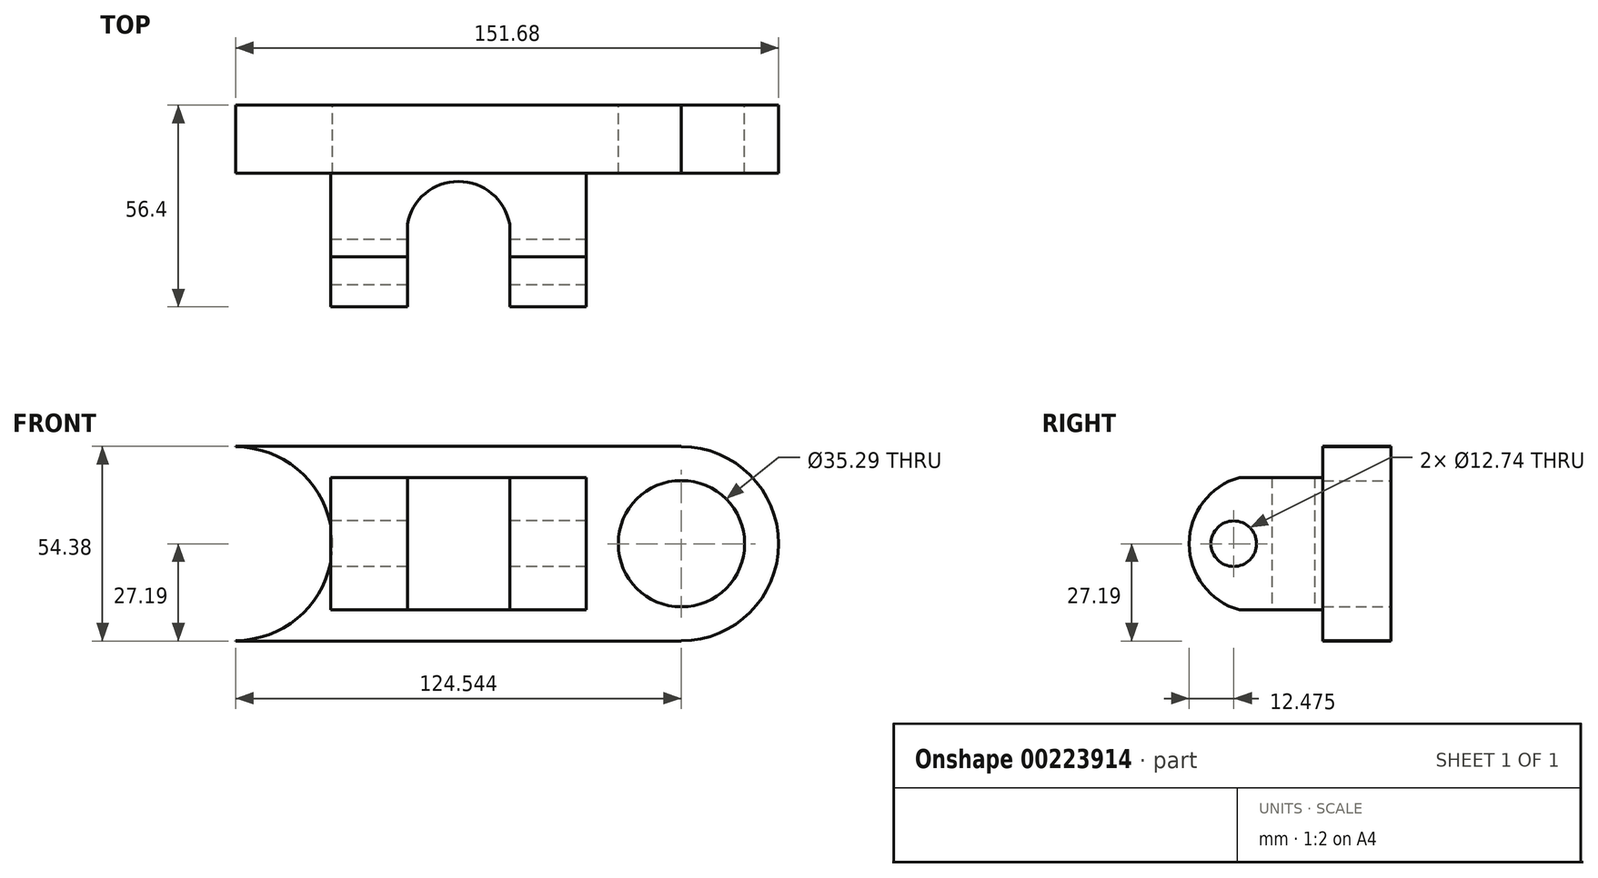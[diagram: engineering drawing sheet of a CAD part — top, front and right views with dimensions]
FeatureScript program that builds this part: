
annotation { "Feature Type Name" : "Feature", "Feature Type Description" : "" }
export const myFeature = defineFeature(function(context is Context, id is Id, definition is map)
    precondition{}
    {
        {
            var Q0;
            Q0=qCreatedBy(makeId("Front.planeOp"),FACE);
            var sketch = newSketch(context, id + "F0", { "sketchPlane" : qUnion([Q0])});
            skLineSegment(sketch, "E0.bottom", {"start": v(-62.27, 27.2) * mm, "end": v(62.27, 27.2) * mm});
            skLineSegment(sketch, "E0.top", {"start": v(-62.27, -27.2) * mm, "end": v(62.27, -27.2) * mm});
            skLineSegment(sketch, "E0.left", {"start": v(-62.27, 27.2) * mm, "end": v(-62.27, -27.2) * mm});
            skLineSegment(sketch, "E0.right", {"start": v(62.27, 27.2) * mm, "end": v(62.27, -27.2) * mm});
            skPoint(sketch, "E0.middle", {"position": v(0, 0) * mm});
            skCircle(sketch, "E1", {"center": v(-62.27, 0) * mm, "radius": 27.08 * mm});
            skCircle(sketch, "E2", {"center": v(62.27, 0) * mm, "radius": 27.13 * mm});
            skCircle(sketch, "E3", {"center": v(-62.27, 0) * mm, "radius": 16.55 * mm});
            skCircle(sketch, "E4", {"center": v(62.27, 0) * mm, "radius": 17.64 * mm});
            skPoint(sketch, "E5.bottom.end.orphan", {"position": v(-23.15, 9.85) * mm});
            skPoint(sketch, "E5.top.end.orphan", {"position": v(-23.15, -9.85) * mm});
            skPoint(sketch, "E5.left.end.orphan", {"position": v(23.15, -9.85) * mm});
            skPoint(sketch, "E5.left.start.orphan", {"position": v(23.15, 9.85) * mm});
            skPoint(sketch, "E6.top.start.orphan", {"position": v(27.33, -15.1) * mm});
            skPoint(sketch, "E6.bottom.start.orphan", {"position": v(27.33, 15.1) * mm});
            skPoint(sketch, "E6.right.end.orphan", {"position": v(-27.33, -15.1) * mm});
            skPoint(sketch, "E6.right.start.orphan", {"position": v(-27.33, 15.1) * mm});
            skSolve(sketch);
        }
        {
            var Q0;
            {var subQ5=sQuery(id+"F0.wireOp",EDGE,"E0.bottom");Q0=makeQuery(id+"F0.imprint","IMPRINT",FACE,{"disambiguationData":[TD([[makeQuery(id+"F0.imprint","IMPRINT",EDGE,{"derivedFrom":subQ5}),-1.0]])]});}
            var Q1;
            {var subQ0=sQuery(id+"F0.wireOp",EDGE,"E1");var subQ1=sQuery(id+"F0.wireOp",EDGE,"E0.left");var subQ2=makeQuery(id+"F0.imprint","INTERSECT",VERTEX,{"disambiguationData":[OD(0.0)],"derivedFrom":[subQ1,subQ0]});Q1=makeQuery(id+"F0.imprint","IMPRINT",FACE,{"disambiguationData":[TD([[makeQuery(id+"F0.imprint","IMPRINT",EDGE,{"disambiguationData":[TD([[subQ2,-1.0]])],"derivedFrom":subQ1}),1.0]])]});}
            var Q2;
            {var subQ0=sQuery(id+"F0.wireOp",EDGE,"E1");var subQ1=sQuery(id+"F0.wireOp",EDGE,"E0.left");var subQ2=makeQuery(id+"F0.imprint","INTERSECT",VERTEX,{"disambiguationData":[OD(0.0)],"derivedFrom":[subQ1,subQ0]});Q2=makeQuery(id+"F0.imprint","IMPRINT",FACE,{"disambiguationData":[TD([[makeQuery(id+"F0.imprint","IMPRINT",EDGE,{"disambiguationData":[TD([[subQ2,-1.0]])],"derivedFrom":subQ1}),-1.0]])]});}
            var Q3;
            {var subQ0=sQuery(id+"F0.wireOp",EDGE,"E2");var subQ1=sQuery(id+"F0.wireOp",EDGE,"E0.right");var subQ2=makeQuery(id+"F0.imprint","INTERSECT",VERTEX,{"disambiguationData":[OD(0.0)],"derivedFrom":[subQ1,subQ0]});Q3=makeQuery(id+"F0.imprint","IMPRINT",FACE,{"disambiguationData":[TD([[makeQuery(id+"F0.imprint","IMPRINT",EDGE,{"disambiguationData":[TD([[subQ2,-1.0]])],"derivedFrom":subQ1}),-1.0]])]});}
            var Q4;
            {var subQ0=sQuery(id+"F0.wireOp",EDGE,"E2");var subQ1=sQuery(id+"F0.wireOp",EDGE,"E0.right");var subQ2=makeQuery(id+"F0.imprint","INTERSECT",VERTEX,{"disambiguationData":[OD(0.0)],"derivedFrom":[subQ1,subQ0]});Q4=makeQuery(id+"F0.imprint","IMPRINT",FACE,{"disambiguationData":[TD([[makeQuery(id+"F0.imprint","IMPRINT",EDGE,{"disambiguationData":[TD([[subQ2,-1.0]])],"derivedFrom":subQ1}),1.0]])]});}
            extrude(context, id + "F1", {"entities" : qUnion([Q0, Q1, Q2, Q3, Q4]), "depth" : 19.05 * mm});
        }
        {
            var Q0;
            Q0=makeQuery(id+"F1.opExtrude","CAP_FACE",FACE,{"disambiguationData":[OSD([sQuery(id+"F0.wireOp",EDGE,"E0.bottom"),sQuery(id+"F0.wireOp",EDGE,"E0.top"),sQuery(id+"F0.wireOp",EDGE,"E0.left"),sQuery(id+"F0.wireOp",EDGE,"E0.right"),sQuery(id+"F0.wireOp",EDGE,"E1"),sQuery(id+"F0.wireOp",EDGE,"E2"),sQuery(id+"F0.wireOp",EDGE,"E3"),sQuery(id+"F0.wireOp",EDGE,"E4")])],"isStart":false});
            var sketch = newSketch(context, id + "F2", { "sketchPlane" : qUnion([Q0])});
            skLineSegment(sketch, "E7.bottom", {"start": v(-35.7, 18.52) * mm, "end": v(35.7, 18.52) * mm});
            skLineSegment(sketch, "E7.top", {"start": v(-35.7, -18.52) * mm, "end": v(35.7, -18.52) * mm});
            skLineSegment(sketch, "E7.left", {"start": v(-35.7, 18.52) * mm, "end": v(-35.7, -18.52) * mm});
            skLineSegment(sketch, "E7.right", {"start": v(35.7, 18.52) * mm, "end": v(35.7, -18.52) * mm});
            skPoint(sketch, "E7.middle", {"position": v(0, 0) * mm});
            skSolve(sketch);
        }
        {
            var Q0;
            Q0 = qSketchRegion(id + "F2", true);
            extrude(context, id + "F3", {"entities" : qUnion([Q0]), "operationType" : NewBodyOperationType.ADD, "depth" : 38.1 * mm});
        }
        {
            var Q0;
            Q0=makeQuery(id+"F3.opExtrude","SWEPT_FACE",FACE,{"disambiguationData":[OSD([sQuery(id+"F2.wireOp",EDGE,"E7.right")])]});
            var sketch = newSketch(context, id + "F4", { "sketchPlane" : qUnion([Q0])});
            skArc(sketch, "E8", {"start": v(-42.34, 18.52) * mm, "mid": v(-56.4, 0) * mm, "end": v(-42.34, -18.52) * mm});
            skSolve(sketch);
        }
        {
            var Q0;
            {var subQ0=sQuery(id+"F4.wireOp",EDGE,"E8");Q0=makeQuery(id+"F4.imprint","IMPRINT",FACE,{"disambiguationData":[TD([[makeQuery(id+"F4.imprint","IMPRINT",EDGE,{"derivedFrom":subQ0}),-1.0]])]});}
            extrude(context, id + "F5", {"entities" : qUnion([Q0]), "operationType" : NewBodyOperationType.REMOVE, "endBound" : BoundingType.THROUGH_ALL, "oppositeDirection" : true, "depth" : 25.4 * mm});
        }
        {
            var Q0;
            Q0=makeQuery(id+"F3.opExtrude","SWEPT_FACE",FACE,{"disambiguationData":[OSD([sQuery(id+"F2.wireOp",EDGE,"E7.top")])]});
            var sketch = newSketch(context, id + "F6", { "sketchPlane" : qUnion([Q0])});
            skLineSegment(sketch, "E9.bottom", {"start": v(-14.3, 60.64) * mm, "end": v(14.3, 60.64) * mm});
            skLineSegment(sketch, "E9.top", {"start": v(-14.3, 33.27) * mm, "end": v(14.3, 33.27) * mm});
            skLineSegment(sketch, "E9.left", {"start": v(-14.3, 60.64) * mm, "end": v(-14.3, 33.27) * mm});
            skLineSegment(sketch, "E9.right", {"start": v(14.3, 60.64) * mm, "end": v(14.3, 33.27) * mm});
            skPoint(sketch, "E9.middle", {"position": v(0, 46.96) * mm});
            skArc(sketch, "E10", {"start": v(-14.3, 33.27) * mm, "mid": v(0, 21.32) * mm, "end": v(14.3, 33.27) * mm});
            skSolve(sketch);
        }
        {
            var Q0;
            {var subQ0=sQuery(id+"F6.wireOp",EDGE,"E9.bottom");Q0=makeQuery(id+"F6.imprint","IMPRINT",FACE,{"disambiguationData":[TD([[makeQuery(id+"F6.imprint","IMPRINT",EDGE,{"derivedFrom":subQ0}),-1.0]])]});}
            var Q1;
            {var subQ0=sQuery(id+"F6.wireOp",EDGE,"E9.top");Q1=makeQuery(id+"F6.imprint","IMPRINT",FACE,{"disambiguationData":[TD([[makeQuery(id+"F6.imprint","IMPRINT",EDGE,{"derivedFrom":subQ0}),1.0]])]});}
            var Q2;
            Q2=makeQuery(id+"F6.imprint","IMPRINT",FACE,{"disambiguationData":[TD([[makeQuery(id+"F6.imprint","IMPRINT",EDGE,{"derivedFrom":sQuery(id+"F6.wireOp",EDGE,"E9.top")}),-1.0]])]});
            extrude(context, id + "F7", {"entities" : qUnion([Q0, Q1, Q2]), "operationType" : NewBodyOperationType.REMOVE, "endBound" : BoundingType.THROUGH_ALL, "oppositeDirection" : true, "depth" : 25.4 * mm});
        }
        {
            var Q0;
            Q0=makeQuery(id+"F3.opExtrude","SWEPT_FACE",FACE,{"disambiguationData":[OSD([sQuery(id+"F2.wireOp",EDGE,"E7.left")])]});
            var sketch = newSketch(context, id + "F8", { "sketchPlane" : qUnion([Q0])});
            skCircle(sketch, "E11", {"center": v(43.92, 0) * mm, "radius": 6.37 * mm});
            skSolve(sketch);
        }
        {
            var Q0;
            Q0 = qSketchRegion(id + "F8", true);
            extrude(context, id + "F9", {"entities" : qUnion([Q0]), "operationType" : NewBodyOperationType.REMOVE, "endBound" : BoundingType.THROUGH_ALL, "oppositeDirection" : true, "depth" : 25.4 * mm});
        }
    });
